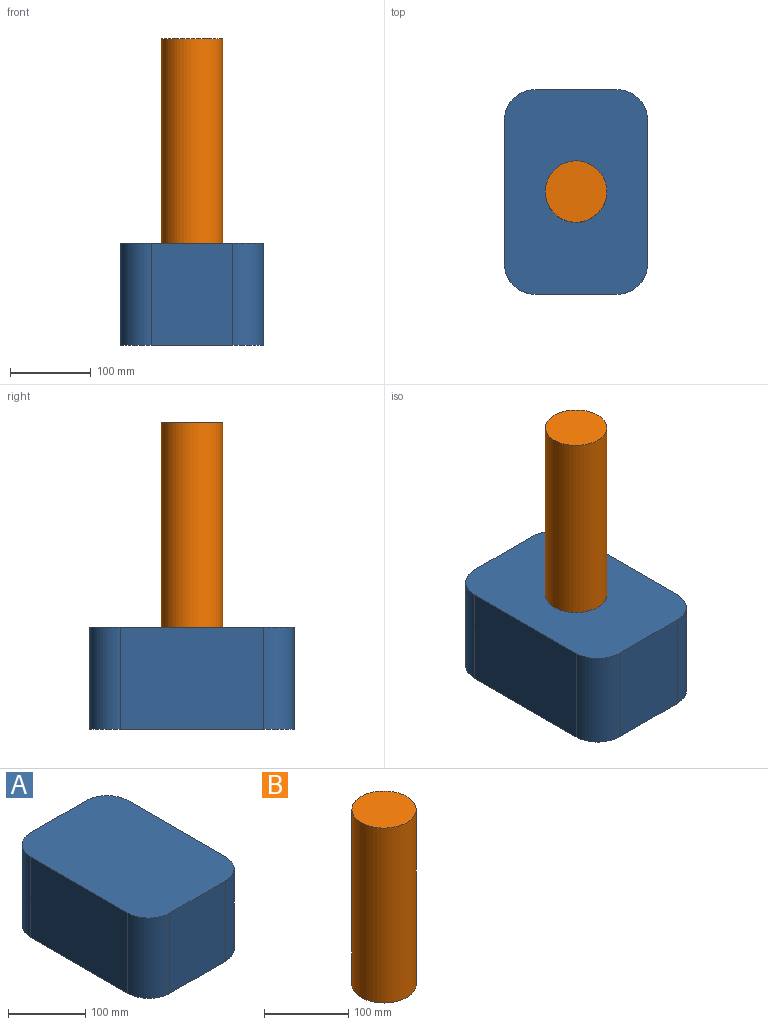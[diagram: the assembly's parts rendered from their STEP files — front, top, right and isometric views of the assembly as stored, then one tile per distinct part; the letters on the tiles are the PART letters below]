
ASSEMBLY  parts=2 mates=1
PART A: 10 faces, bbox 177.8x254x127 mm
  f0: plane 177.8x127mm, normal (-1,0,0), area 22580.6mm2, adj f1,f3,f7,f9
  f1: plane 254x177.8mm, normal (0,0,-1), area 43915.1mm2, adj f0,f2,f4,f5,f6,f7,f8,f9
  f2: plane 177.8x127mm, normal (1,0,0), area 22580.6mm2, adj f1,f3,f6,f8
  f3: plane 254x177.8mm, normal (0,0,1), area 43915.1mm2, adj f0,f2,f4,f5,f6,f7,f8,f9
  f4: plane 127x101.6mm, normal (0,-1,0), area 12903.2mm2, adj f1,f3,f8,f9
  f5: plane 127x101.6mm, normal (0,1,0), area 12903.2mm2, adj f1,f3,f6,f7
  f6: cylinder r=38.1mm len=127mm, axis (0,0,1), area 7600.6mm2, adj f1,f2,f3,f5
  f7: cylinder r=38.1mm len=127mm, axis (0,0,-1), area 7600.6mm2, adj f0,f1,f3,f5
  f8: cylinder r=38.1mm len=127mm, axis (0,0,-1), area 7600.6mm2, adj f1,f2,f3,f4
  f9: cylinder r=38.1mm len=127mm, axis (0,0,1), area 7600.6mm2, adj f0,f1,f3,f4
PART B: 3 faces, bbox 76.2x76.2x254 mm
  f0: cylinder r=38.1mm len=254mm, axis (0,0,-1), area 60804.9mm2, adj f1,f2
  f1: plane 76.2x76.2mm, normal (0,0,1), area 4560.4mm2, adj f0
  f2: plane 76.2x76.2mm, normal (0,0,-1), area 4560.4mm2, adj f0
PLACE A t=(-83.21,219.8,-272.77)mm
PLACE B t=(5.69,92.8,-145.77)mm
MATE planar A.f3 <-> B.f0  axis (0,0,1) through (5.69,92.8,-145.77)mm
